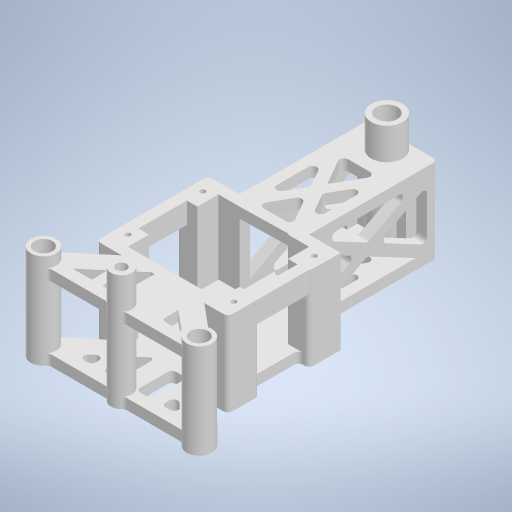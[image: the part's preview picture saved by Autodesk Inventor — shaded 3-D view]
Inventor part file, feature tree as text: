
AUTODESK INVENTOR PART (.ipt)
format: ipt  version: 2023 (Build 270158000, 158)  size: 1,315,328 bytes
history: native  units: mm
features: projected_geometry x33, extrude x15, sketch x11, fillet x3
ambient origin geometry x8: Origin, YZ Plane, XZ Plane, XY Plane, X Axis, Y Axis, Z Axis, Center Point
bodies: Body1 (feature_tree)
feature tree (62):
  sketch  "Sketch1"  dims[d0=43.0mm d1=43.0mm]
  extrude  "Extrusion5"  Depth=43.0mm
  extrude  "Extrusion6"  Depth=53.0mm
  extrude  "Extrusion7"  Depth=10.0mm
  extrude  "Extrusion11"  Depth=5.0mm
  extrude  "Extrusion12"  Depth=53.0mm
  extrude  "Extrusion13"  Depth=5.0mm
  extrude  "Extrusion14"  Depth=10.0mm
  extrude  "Extrusion15"  Depth=15.0mm
  extrude  "Extrusion16"  Depth=35.0mm TaperAngle=0.0deg
  extrude  "Extrusion17"  Depth=10.0mm
  extrude  "Extrusion18"  Depth=10.0mm
  extrude  "Extrusion19"  Depth=15.0mm
  extrude  "Extrusion20"  Depth=2.5mm
  extrude  "Extrusion21"  Depth=2.5mm
  fillet  "Fillet3"  Radius=2.5mm
  fillet  "Fillet4"  Radius=2.5mm
  fillet  "Fillet5"  Radius=15.0mm
  extrude  "Extrusion22"  Depth=0.5mm
  sketch  "Sketch2"  dims[d2=53.0mm d3=53.0mm]
  projected_geometry  "Projected Loop1"
  projected_geometry  "Projected Loop2"
  projected_geometry  "Projected Loop3"
  projected_geometry  "Projected Loop4"
  sketch  "Sketch8"  dims[d4=15.0mm d5=10.0mm]
  projected_geometry  "Projected Loop10"
  projected_geometry  "Projected Loop11"
  projected_geometry  "Projected Loop12"
  projected_geometry  "Projected Loop13"
  sketch  "Sketch10"  dims[d7=5.0mm d8=27.0mm]
  projected_geometry  "Projected Loop14"
  projected_geometry  "Projected Loop15"
  sketch  "Sketch11"  dims[d9=10.0mm d10=53.0mm]
  projected_geometry  "Projected Loop16"
  projected_geometry  "Projected Loop17"
  projected_geometry  "Projected Loop18"
  projected_geometry  "Projected Loop19"
  projected_geometry  "Projected Loop20"
  sketch  "Sketch12"  dims[d11=53.0mm d12=5.0mm]
  sketch  "Sketch13"  dims[d13=27.0mm d23=10.0mm]
  projected_geometry  "Projected Loop21"
  projected_geometry  "Projected Loop22"
  projected_geometry  "Projected Loop23"
  sketch  "Sketch14"  dims[d25=15.0mm d28=77.457754mm]
  projected_geometry  "Projected Loop24"
  projected_geometry  "Projected Loop25"
  projected_geometry  "Projected Loop26"
  projected_geometry  "Projected Loop27"
  projected_geometry  "Projected Loop28"
  sketch  "Sketch16"  dims[d29=5.0mm d30=0.0mm d31=35.0mm d32=0.0mm]
  projected_geometry  "Projected Loop29"
  projected_geometry  "Projected Loop30"
  projected_geometry  "Projected Loop31"
  sketch  "Sketch18"  dims[d34=5.0mm d35=10.0mm]
  projected_geometry  "Projected Loop34"
  projected_geometry  "Projected Loop35"
  projected_geometry  "Projected Loop36"
  projected_geometry  "Projected Loop37"
  projected_geometry  "Projected Loop38"
  projected_geometry  "Projected Loop39"
  sketch  "Sketch20"  dims[d37=15.0mm d38=10.0mm d39=15.0mm d40=2.5mm d41=2.5mm d42=2.5mm d43=2.5mm d44=15.0mm d45=0.0mm d60=48.849mm d61=5.0mm d62=50.0mm d63=10.0mm d64=74.0mm d65=8.0mm d66=12.0mm d68=8.0mm d69=5.0mm d70=35.0mm d71=0.0mm d72=5.0mm d73=0.0mm d74=17.103mm d75=10.0mm d76=5.0mm d77=0.0mm d78=0.0mm d81=8.5mm d83=5.0mm d84=2.5mm d85=2.5mm d86=2.5mm d87=2.5mm d88=5.0mm d89=0.0mm d95=5.0mm d96=0.0mm d97=5.0mm d98=5.0mm d99=10.0mm d100=0.0mm d101=5.0mm d102=5.0mm d103=5.0mm d104=0.0mm d105=2.0mm d106=0.0mm d107=5.0mm d108=0.0mm d109=5.0mm d110=10.0mm d111=25.0mm d112=0.0mm d113=5.0mm d114=10.0mm d115=25.0mm d116=0.0mm d117=2.0mm d118=2.0mm d119=2.0mm d121=8.5mm d122=8.5mm d123=5.0mm d124=0.0mm d22=0.5mm d24=0.5mm d55=0.5mm d56=0.872665mm d57=0.5mm d58=0.872665mm]
  projected_geometry  "Projected Loop40"
